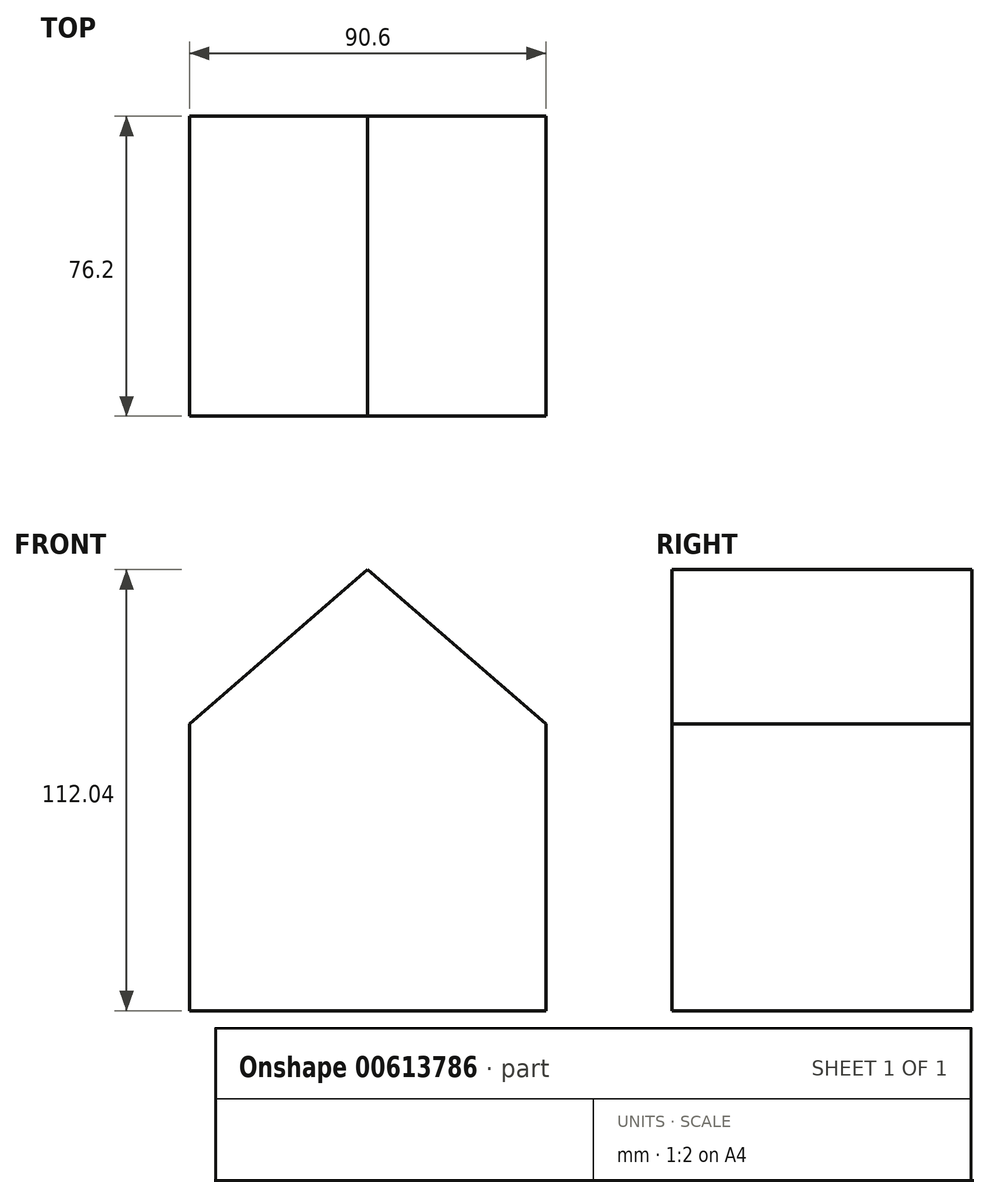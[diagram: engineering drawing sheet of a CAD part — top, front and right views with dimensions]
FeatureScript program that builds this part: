
annotation { "Feature Type Name" : "Feature", "Feature Type Description" : "" }
export const myFeature = defineFeature(function(context is Context, id is Id, definition is map)
    precondition{}
    {
        {
            var Q0;
            Q0=qCreatedBy(makeId("Front.planeOp"),FACE);
            var sketch = newSketch(context, id + "F0", { "sketchPlane" : qUnion([Q0])});
            skLineSegment(sketch, "E0.bottom", {"start": v(-45.3, 36.45) * mm, "end": v(45.3, 36.45) * mm});
            skLineSegment(sketch, "E0.top", {"start": v(-45.3, -36.45) * mm, "end": v(45.3, -36.45) * mm});
            skLineSegment(sketch, "E0.left", {"start": v(-45.3, 36.45) * mm, "end": v(-45.3, -36.45) * mm});
            skLineSegment(sketch, "E0.right", {"start": v(45.3, 36.45) * mm, "end": v(45.3, -36.45) * mm});
            skPoint(sketch, "E0.middle", {"position": v(0, 0) * mm});
            skLineSegment(sketch, "E1", {"start": v(-45.3, 36.45) * mm, "end": v(0, 75.59) * mm});
            skLineSegment(sketch, "E2", {"start": v(0, 75.59) * mm, "end": v(45.3, 36.45) * mm});
            skLineSegment(sketch, "E3.bottom", {"start": v(-9.38, 29.22) * mm, "end": v(9.11, 29.22) * mm});
            skLineSegment(sketch, "E3.top", {"start": v(-9.38, 57.63) * mm, "end": v(9.11, 57.63) * mm});
            skLineSegment(sketch, "E3.left", {"start": v(-9.38, 29.22) * mm, "end": v(-9.38, 57.63) * mm});
            skLineSegment(sketch, "E3.right", {"start": v(9.11, 29.22) * mm, "end": v(9.11, 57.63) * mm});
            skSolve(sketch);
        }
        {
            var Q0;
            Q0 = qSketchRegion(id + "F0", true);
            var Q1;
            {var subQ5=sQuery(id+"F0.wireOp",EDGE,"E3.top");Q1=makeQuery(id+"F0.imprint","IMPRINT",FACE,{"disambiguationData":[TD([[makeQuery(id+"F0.imprint","IMPRINT",EDGE,{"derivedFrom":subQ5}),-1.0]])]});}
            var Q2;
            {var subQ5=sQuery(id+"F0.wireOp",EDGE,"E3.bottom");Q2=makeQuery(id+"F0.imprint","IMPRINT",FACE,{"disambiguationData":[TD([[makeQuery(id+"F0.imprint","IMPRINT",EDGE,{"derivedFrom":subQ5}),1.0]])]});}
            extrude(context, id + "F1", {"entities" : qUnion([Q0, Q1, Q2]), "depth" : 76.2 * mm, "offsetDistance" : 25.4 * mm, "symmetric" : true});
        }
    });
